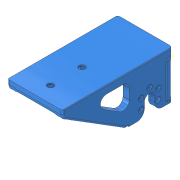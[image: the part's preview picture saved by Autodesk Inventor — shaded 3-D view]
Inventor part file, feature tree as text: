
AUTODESK INVENTOR PART (.ipt)
format: ipt  version: 2018 (Build 220112000, 112)  size: 1,385,472 bytes
history: native  units: in
note: dims shown in document units (in); Inventor stores cm internally (conversion verified against a paired STEP export)
features: sketch x51, extrude x45, fillet x26, reference x18, projected_geometry x15, hole x5, mirror x4, other x3, plane x1, pattern_circular x1
ambient origin geometry x8: Origin, YZ Plane, XZ Plane, XY Plane, X Axis, Y Axis, Z Axis, Center Point
bodies: Solid1 (feature_tree)
feature tree (169):
  extrude  "Extrusion1"  Depth=1.75in
  fillet  "Fillet1"  Radius=1.358in
  extrude  "Extrusion2"  Depth=0.196in
  fillet  "Fillet2"  Radius=1.5in
  extrude  "Extrusion3"  Depth=3.5in TaperAngle=0.0deg
  extrude  "Extrusion4"  Depth=0.125in
  hole  "Hole1"  [1 undecoded]
  extrude  "Extrusion5"  Depth=0.25in
  extrude  "Extrusion6"  Depth=0.125in
  hole  "Hole2"  [1 undecoded]
  fillet  "Fillet4"  Radius=0.188in
  extrude  "Extrusion7"  Depth=0.3125in
  fillet  "Fillet5"  Radius=0.1875in
  fillet  "Fillet6"  Radius=0.3125in
  extrude  "Extrusion8"  Depth=3.5in TaperAngle=0.0deg
  extrude  "Extrusion9"  Depth=3.5in TaperAngle=0.0deg
  extrude  "Extrusion10"  Depth=0.325in
  fillet  "Fillet7"  Radius=3.5in
  fillet  "Fillet8"  Radius=3.5in
  fillet  "Fillet9"  Radius=0.125in
  fillet  "Fillet10"  Radius=1.375in
  extrude  "Extrusion11"  Depth=3.5in TaperAngle=0.0deg
  extrude  "Extrusion12"  Depth=0.2in
  fillet  "Fillet11"  Radius=2.0in
  hole  "Hole3"  [1 undecoded]
  extrude  "Extrusion13"  TaperAngle=0.0deg  [1 undecoded]
  extrude  "Extrusion14"  Depth=0.0625in
  fillet  "Fillet12"  Radius=0.5in
  extrude  "Extrusion15"  Depth=0.0625in
  extrude  "Extrusion16"  Depth=2.0in TaperAngle=0.0deg
  fillet  "Fillet13"  Radius=1.0in
  fillet  "Fillet14"  Radius=2.0in
  extrude  "Extrusion17"  Depth=0.5in
  fillet  "Fillet15"  Radius=0.3125in
  fillet  "Fillet16"  Radius=0.3125in
  fillet  "Fillet17"  Radius=0.5in
  extrude  "Extrusion18"  Depth=0.5in
  extrude  "Extrusion19"  Depth=0.3125in
  extrude  "Extrusion20"  Depth=1.2436in
  extrude  "Extrusion21"  Depth=0.5in
  extrude  "Extrusion22"  Depth=0.5in
  fillet  "Fillet18"  Radius=0.165in
  fillet  "Fillet19"  Radius=0.75in
  fillet  "Fillet20"  Radius=4.0in
  fillet  "Fillet21"  Radius=0.0156in
  fillet  "Fillet22"  Radius=4.0in
  hole  "Hole4"  [1 undecoded]
  fillet  "Fillet23"  Radius=0.0312in
  extrude  "Extrusion23"  Depth=0.25in
  sketch  "Sketch28"  dims[d109=4.0in d110=0.0in d111=0.0625in d112=0.0312in]
  extrude  "Extrusion24"  Depth=1.5in
  extrude  "Extrusion25"  Depth=4.0in TaperAngle=0.0deg
  plane  "Work Plane1"
  mirror  "Mirror1"
  extrude  "Extrusion26"  Depth=0.25in
  mirror  "Mirror2"
  extrude  "Extrusion27"  TaperAngle=0.0deg  [1 undecoded]
  extrude  "Extrusion28"  Depth=4.0in TaperAngle=0.0deg
  mirror  "Mirror3"
  fillet  "Fillet24"  Radius=4.0in
  extrude  "Extrusion29"  Depth=0.2in
  extrude  "Extrusion30"  Depth=0.1in TaperAngle=0.0deg
  mirror  "Mirror4"
  extrude  "Extrusion31"  Depth=0.125in
  sketch  "Sketch37"  dims[d136=0.125in d137=0.25in]
  extrude  "Extrusion32"  Depth=0.5in
  extrude  "Extrusion33"  Depth=0.0625in
  pattern_circular  "Circular Pattern1"  [2 undecoded]
  extrude  "Extrusion34"  Depth=0.125in TaperAngle=0.0deg
  extrude  "Extrusion35"  Depth=0.125in
  fillet  "Fillet25"  Radius=0.125in
  extrude  "Extrusion36"  Depth=0.125in
  extrude  "Extrusion37"  Depth=0.5in
  extrude  "Extrusion38"  Depth=0.125in TaperAngle=0.0deg
  extrude  "Extrusion39"  Depth=0.125in
  extrude  "Extrusion40"  Depth=0.125in TaperAngle=0.0deg
  fillet  "Fillet26"  Radius=0.01in
  extrude  "Extrusion41"  Depth=0.125in
  hole  "Hole5"  [1 undecoded]
  extrude  "Extrusion42"  Depth=0.125in
  fillet  "Fillet27"  Radius=1.0in
  extrude  "Extrusion43"  Depth=0.125in TaperAngle=0.0deg
  extrude  "Extrusion44"  Depth=0.125in TaperAngle=360.0deg
  extrude  "Extrusion45"  Depth=0.125in TaperAngle=0.0deg
  sketch  "Sketch1"  dims[d0=0.25in d1=1.75in d2=1.358in]
  sketch  "Sketch2"  dims[d3=0.196in d4=0.196in d5=1.5in]
  sketch  "Sketch3"  dims[d6=1.5in d7=3.5in d8=0.0in]
  sketch  "Sketch4"  dims[d9=0.125in d10=0.625in]
  projected_geometry  "Projected Loop1"
  sketch  "Sketch5"  dims[d11=0.5625in d12=0.5625in]
  reference  "Reference1"
  reference  "Reference2"
  reference  "Reference3"
  reference  "Reference4"
  reference  "Reference5"
  reference  "Reference6"
  reference  "Reference7"
  reference  "Reference8"
  reference  "Reference9"
  reference  "Reference10"
  reference  "Reference11"
  reference  "Reference12"
  reference  "Reference13"
  sketch  "Sketch6"  dims[d13=0.25in d14=0.25in]
  reference  "Reference14"
  reference  "Reference15"
  reference  "Reference16"
  reference  "Reference17"
  reference  "Reference18"
  sketch  "Sketch7"  dims[d15=0.125in d16=0.125in]
  sketch  "Sketch8"  dims[d17=3.5in d18=0.0in d19=0.0625in d20=0.188in]
  sketch  "Sketch9"  dims[d21=0.188in d22=0.3125in d23=0.1875in d24=0.3125in]
  sketch  "Sketch10"  dims[d25=0.1875in d26=3.5in d27=0.0in]
  projected_geometry  "Projected Loop2"
  sketch  "Sketch11"  dims[d28=2.0in d29=3.5in d30=0.0in]
  sketch  "Sketch12"  dims[d32=0.15in d33=0.75in d34=0.279in d35=0.25in d36=0.5635in d37=1.0in d38=0.8108in d39=0.325in d40=3.5in d41=0.0in d42=3.5in d43=0.0in]
  sketch  "Sketch13"  dims[d44=0.17in d45=0.75in d46=0.279in d47=0.25in d48=0.5635in d49=4.0in d50=0.8108in d51=0.125in d52=1.375in]
  sketch  "Sketch14"  dims[d53=0.375in d54=3.5in d55=0.0in]
  sketch  "Sketch15"  dims[d56=0.2in d57=0.2in d58=2.0in d59=0.0in]
  sketch  "Sketch16"  dims[d60=0.375in d61=0.5in]
  sketch  "Sketch17"  dims[d63=2.0in d64=0.0in d65=0.0in]
  sketch  "Sketch18"  dims[d66=2.0in d67=0.0in d68=0.0625in d69=0.5in]
  sketch  "Sketch19"  dims[d70=0.0625in d71=0.0625in]
  projected_geometry  "Projected Loop3"
  sketch  "Sketch20"  dims[d72=1.0in d73=2.0in d74=0.0in d75=1.0in d76=2.0in d77=0.0in]
  sketch  "Sketch21"  dims[d78=0.0625in d80=2.0in d81=0.3125in d82=0.3125in d83=0.5in]
  sketch  "Sketch22"  dims[d84=0.5in d85=0.3125in]
  sketch  "Sketch23"  dims[d86=0.3125in d87=0.3125in]
  sketch  "Sketch24"  dims[d88=0.3125in d89=1.2436in]
  sketch  "Sketch25"  dims[d90=1.2436in]
  projected_geometry  "Projected Loop4"
  projected_geometry  "Projected Loop5"
  sketch  "Sketch26"  dims[d91=0.194in d92=0.75in d93=0.332in d94=0.188in d95=0.5635in d96=1.0in d97=0.8108in d98=0.5in]
  sketch  "Sketch27"  dims[d99=0.5in d100=0.5in d101=0.165in d102=0.0in d103=0.75in d104=4.0in d105=0.0in d106=0.0156in d107=4.0in d108=0.0in]
  projected_geometry  "Projected Loop6"
  sketch  "Sketch29"  dims[d113=0.25in d114=0.25in]
  sketch  "Sketch30"  dims[d115=0.75in d116=1.5in]
  sketch  "Sketch31"  dims[d117=0.875in d118=4.0in d119=0.0in]
  projected_geometry  "Projected Loop7"
  sketch  "Sketch32"  dims[d120=0.25in d121=0.25in]
  sketch  "Sketch33"  dims[d122=0.0156in d123=0.0in]
  projected_geometry  "Projected Loop8"
  sketch  "Sketch34"  dims[d124=4.0in d125=0.0in d126=4.0in d127=0.0in d128=4.0in d129=0.0in]
  sketch  "Sketch35"  dims[d130=0.2in d131=0.2in]
  sketch  "Sketch36"  dims[d132=2.0in d133=0.0in d134=0.1in d135=0.0in]
  sketch  "Sketch38"  dims[d138=0.25in d139=0.5in]
  sketch  "Sketch39"  dims[d140=0.0625in d141=2.0in]
  sketch  "Sketch40"  dims[d142=0.625in]
  sketch  "Sketch41"  dims[d143=0.75in d144=0.75in d145=0.375in d146=0.25in d147=0.5635in d148=4.0in d149=0.8108in]
  sketch  "Sketch42"  dims[d150=0.0208in]
  sketch  "Sketch43"  dims[d151=1.0in d152=0.0in]
  sketch  "Sketch44"  dims[d153=1.0in d154=0.0in]
  sketch  "Sketch45"  dims[d155=0.5in]
  sketch  "Sketch46"  dims[d156=0.5in]
  projected_geometry  "Projected Loop9"
  projected_geometry  "Projected Loop10"
  projected_geometry  "Projected Loop11"
  sketch  "Sketch47"  dims[d157=0.25in d158=0.0in]
  sketch  "Sketch48"  dims[d159=0.25in d160=0.0in]
  projected_geometry  "Projected Loop12"
  sketch  "Sketch49"  dims[d161=0.311in]
  sketch  "Sketch50"  dims[d165=1.9in]
  projected_geometry  "Projected Loop13"
  projected_geometry  "Projected Loop14"
  projected_geometry  "Projected Loop15"
  sketch  "Sketch51"  dims[d166=0.5909in d167=0.5909in d168=4.0in d169=0.0in d170=0.1in d171=0.125in d172=0.0in d173=0.25in d175=0.5in d176=1.0in d177=0.0in d178=0.75in d179=1.0in d180=0.0in d181=0.01in d182=0.01in d183=1.0in d184=0.0in d185=0.17in d186=1.0in d187=0.0in d188=1.0in d189=0.0in d190=2.3622in d191=360.0deg d193=1.0in d194=0.0in d195=0.0in d196=5.0in d197=0.0in d198=0.125in d199=0.164in d200=0.375in d201=0.2in d202=0.164in d203=0.375in d204=0.2in d205=5.0in d206=0.0in d208=5.0in d209=0.0in d210=0.2in d211=0.2in d212=1.045in d213=1.0in d214=0.0in d215=1.0in d216=0.0in d217=0.0in d218=1.0in d219=0.0in d220=0.05in d221=1.0in d222=0.0in d223=0.875in d224=0.875in d225=1.0in d226=1.1811in d228=1.0in d229=0.3937in d231=1.0in d233=0.194in d234=0.75in d235=0.5in d236=0.11in d237=0.5635in d238=1.0in d239=0.8108in d240=0.75in d241=0.75in d242=0.75in d243=0.15in d244=0.0in d245=0.125in d246=0.188in d247=0.0in d248=0.051in d249=0.0in d250=0.05in d251=0.0in]
  parser-record x1  (decoder bookkeeping rows leaked as tree rows — omitted from the tree; the rows remain in map.json)
  other  "Assembly3.iam"
  other  "REV-41-1300:1"
note: 9 required parameter values undecoded (feature->parameter linkage not recoverable at this tier; creation-order binding heuristic only, values carry confidence <= 0.55)
note: 1 file-system path scrubbed to <path> (originals preserved in map.json)
